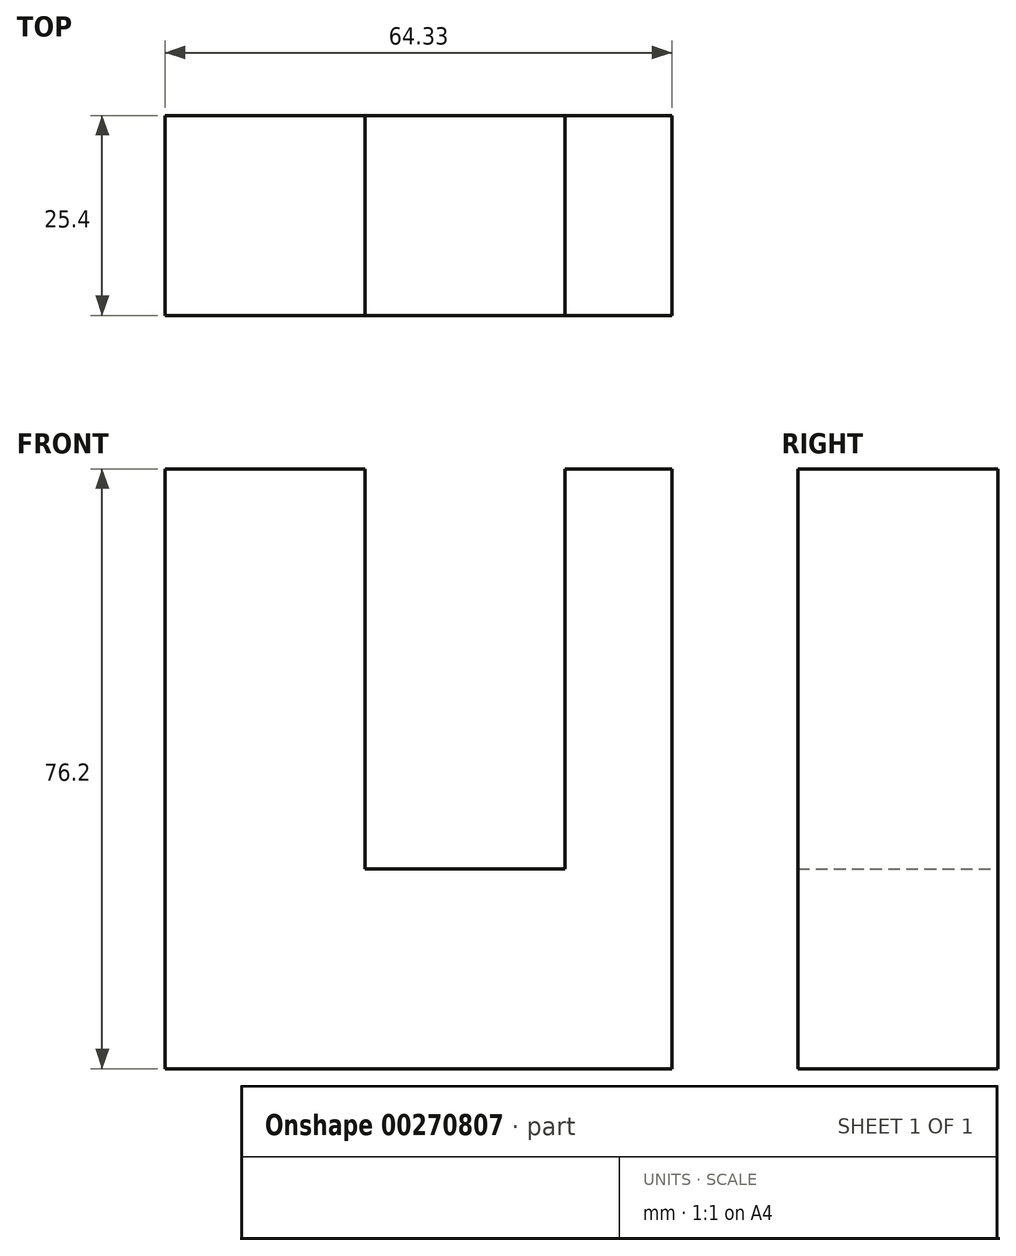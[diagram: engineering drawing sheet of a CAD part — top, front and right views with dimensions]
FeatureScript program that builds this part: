
annotation { "Feature Type Name" : "Feature", "Feature Type Description" : "" }
export const myFeature = defineFeature(function(context is Context, id is Id, definition is map)
    precondition{}
    {
        {
            var Q0;
            Q0=qCreatedBy(makeId("Front.planeOp"),FACE);
            var sketch = newSketch(context, id + "F0", { "sketchPlane" : qUnion([Q0])});
            skLineSegment(sketch, "E0", {"start": v(0, 0) * mm, "end": v(-64.33, 0) * mm});
            skLineSegment(sketch, "E1", {"start": v(-64.33, 0) * mm, "end": v(-64.33, 76.2) * mm});
            skLineSegment(sketch, "E2", {"start": v(-64.33, 76.2) * mm, "end": v(-38.93, 76.2) * mm});
            skLineSegment(sketch, "E3", {"start": v(-38.93, 76.2) * mm, "end": v(-38.93, 25.4) * mm});
            skLineSegment(sketch, "E4", {"start": v(-38.93, 25.4) * mm, "end": v(-13.53, 25.4) * mm});
            skLineSegment(sketch, "E5", {"start": v(-13.53, 25.4) * mm, "end": v(-13.53, 76.2) * mm});
            skLineSegment(sketch, "E6", {"start": v(-13.53, 76.2) * mm, "end": v(0, 76.2) * mm});
            skLineSegment(sketch, "E7", {"start": v(0, 0) * mm, "end": v(0, 76.2) * mm});
            skSolve(sketch);
        }
        {
            var Q0;
            Q0=makeQuery(id+"F0.imprint","IMPRINT",FACE,{"disambiguationData":[TD([[makeQuery(id+"F0.imprint","IMPRINT",EDGE,{"derivedFrom":sQuery(id+"F0.wireOp",EDGE,"E0")}),-1.0]])]});
            extrude(context, id + "F1", {"entities" : qUnion([Q0]), "depth" : 25.4 * mm});
        }
    });
